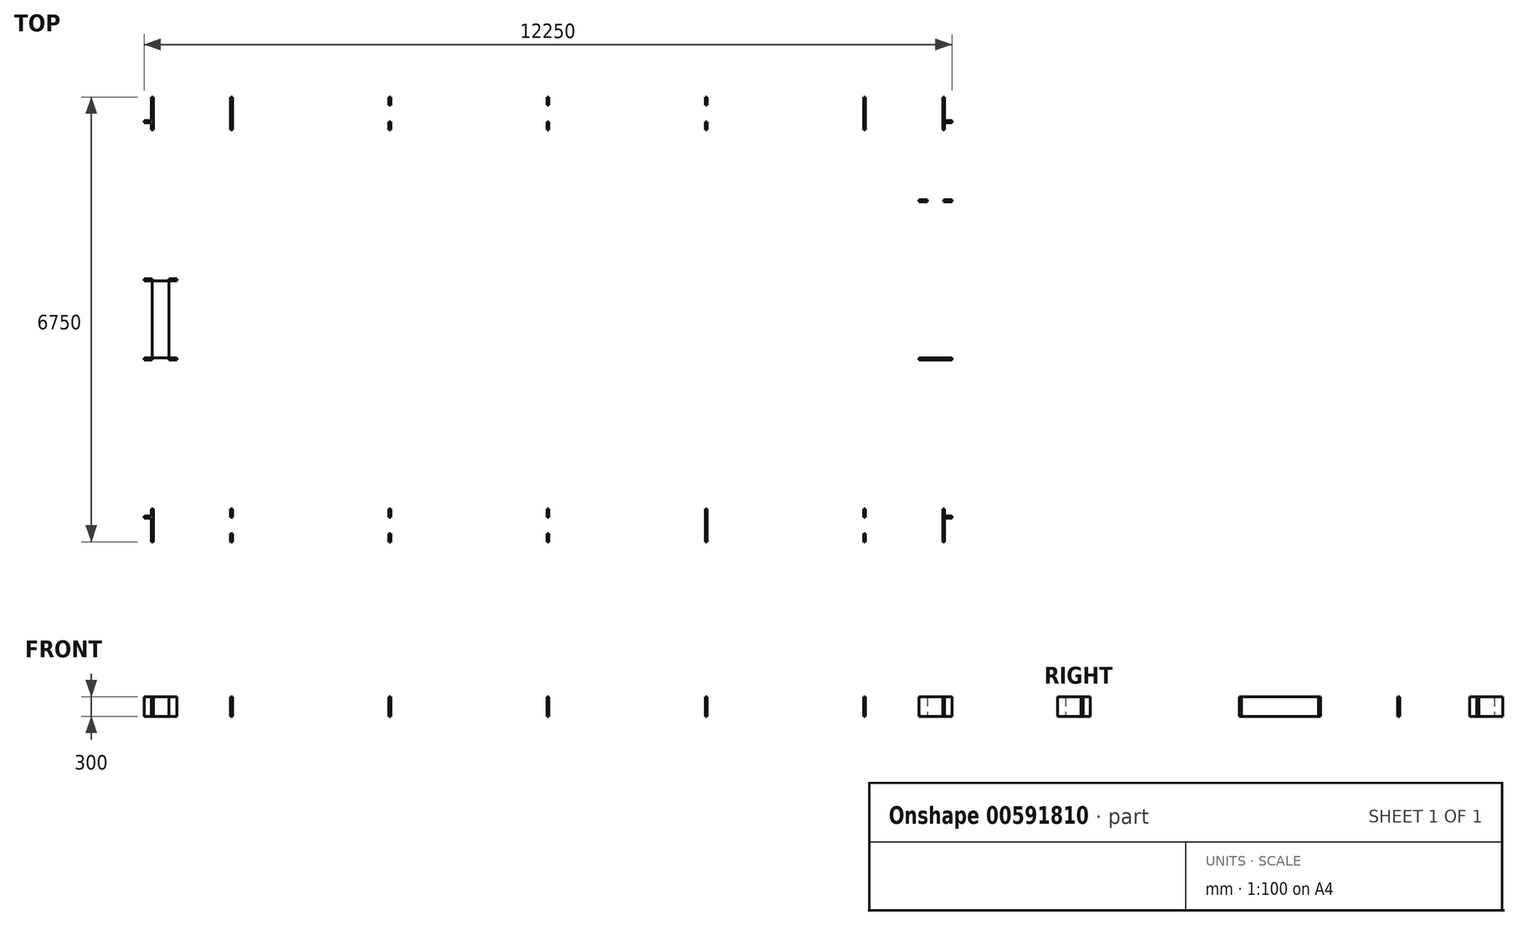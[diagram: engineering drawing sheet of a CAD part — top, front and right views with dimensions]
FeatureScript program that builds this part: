
annotation { "Feature Type Name" : "Feature", "Feature Type Description" : "" }
export const myFeature = defineFeature(function(context is Context, id is Id, definition is map)
    precondition{}
    {
        {
            var Q0;
            Q0=qCreatedBy(makeId("Top.planeOp"),FACE);
            var sketch = newSketch(context, id + "F0", { "sketchPlane" : qUnion([Q0]), "disableImprinting" : false});
            skLineSegment(sketch, "E0.bottom", {"start": v(-5814.67, 3025.3) * mm, "end": v(5685.33, 3025.3) * mm});
            skLineSegment(sketch, "E0.top", {"start": v(-5814.67, -2974.7) * mm, "end": v(5685.33, -2974.7) * mm});
            skLineSegment(sketch, "E0.left", {"start": v(-5814.67, 3025.3) * mm, "end": v(-5814.67, -2974.7) * mm});
            skLineSegment(sketch, "E0.right", {"start": v(5685.33, 3025.3) * mm, "end": v(5685.33, -2974.7) * mm});
            skLineSegment(sketch, "E1.bottom", {"start": v(-5814.67, 3025.3) * mm, "end": v(-6064.67, 3025.3) * mm});
            skLineSegment(sketch, "E1.top", {"start": v(-5814.67, 625.3) * mm, "end": v(-6064.67, 625.3) * mm});
            skLineSegment(sketch, "E1.left", {"start": v(-5814.67, 3025.3) * mm, "end": v(-5814.67, 625.3) * mm});
            skLineSegment(sketch, "E1.right", {"start": v(-6064.67, 3025.3) * mm, "end": v(-6064.67, 625.3) * mm});
            skLineSegment(sketch, "E2.bottom", {"start": v(-6064.67, 625.3) * mm, "end": v(-5814.67, 625.3) * mm});
            skLineSegment(sketch, "E2.top", {"start": v(-6064.67, -574.7) * mm, "end": v(-5814.67, -574.7) * mm});
            skLineSegment(sketch, "E2.left", {"start": v(-6064.67, 625.3) * mm, "end": v(-6064.67, -574.7) * mm});
            skLineSegment(sketch, "E2.right", {"start": v(-5814.67, 625.3) * mm, "end": v(-5814.67, -574.7) * mm});
            skLineSegment(sketch, "E3.bottom", {"start": v(-5814.67, -574.7) * mm, "end": v(-6064.67, -574.7) * mm});
            skLineSegment(sketch, "E3.top", {"start": v(-5814.67, -2974.7) * mm, "end": v(-6064.67, -2974.7) * mm});
            skLineSegment(sketch, "E3.left", {"start": v(-5814.67, -574.7) * mm, "end": v(-5814.67, -2974.7) * mm});
            skLineSegment(sketch, "E3.right", {"start": v(-6064.67, -574.7) * mm, "end": v(-6064.67, -2974.7) * mm});
            skLineSegment(sketch, "E4.bottom", {"start": v(-6064.67, -2974.7) * mm, "end": v(-4864.67, -2974.7) * mm});
            skLineSegment(sketch, "E4.top", {"start": v(-6064.67, -3224.7) * mm, "end": v(-4864.67, -3224.7) * mm});
            skLineSegment(sketch, "E4.left", {"start": v(-6064.67, -2974.7) * mm, "end": v(-6064.67, -3224.7) * mm});
            skLineSegment(sketch, "E4.right", {"start": v(-4864.67, -2974.7) * mm, "end": v(-4864.67, -3224.7) * mm});
            skLineSegment(sketch, "E5.bottom", {"start": v(-4864.67, -2974.7) * mm, "end": v(-2464.67, -2974.7) * mm});
            skLineSegment(sketch, "E5.top", {"start": v(-4864.67, -3224.7) * mm, "end": v(-2464.67, -3224.7) * mm});
            skLineSegment(sketch, "E5.right", {"start": v(-2464.67, -2974.7) * mm, "end": v(-2464.67, -3224.7) * mm});
            skLineSegment(sketch, "E6.bottom", {"start": v(5685.33, -2974.7) * mm, "end": v(5935.33, -2974.7) * mm});
            skLineSegment(sketch, "E6.top", {"start": v(5685.33, -574.7) * mm, "end": v(5935.33, -574.7) * mm});
            skLineSegment(sketch, "E6.left", {"start": v(5685.33, -2974.7) * mm, "end": v(5685.33, -574.7) * mm});
            skLineSegment(sketch, "E6.right", {"start": v(5935.33, -2974.7) * mm, "end": v(5935.33, -574.7) * mm});
            skLineSegment(sketch, "E7.bottom", {"start": v(5935.33, -2974.7) * mm, "end": v(4735.33, -2974.7) * mm});
            skLineSegment(sketch, "E7.top", {"start": v(5935.33, -3224.7) * mm, "end": v(4735.33, -3224.7) * mm});
            skLineSegment(sketch, "E7.left", {"start": v(5935.33, -2974.7) * mm, "end": v(5935.33, -3224.7) * mm});
            skLineSegment(sketch, "E7.right", {"start": v(4735.33, -2974.7) * mm, "end": v(4735.33, -3224.7) * mm});
            skLineSegment(sketch, "E8.bottom", {"start": v(4735.33, -2974.7) * mm, "end": v(2335.33, -2974.7) * mm});
            skLineSegment(sketch, "E8.top", {"start": v(4735.33, -3224.7) * mm, "end": v(2335.33, -3224.7) * mm});
            skLineSegment(sketch, "E8.right", {"start": v(2335.33, -2974.7) * mm, "end": v(2335.33, -3224.7) * mm});
            skLineSegment(sketch, "E9.bottom", {"start": v(2335.33, -2974.7) * mm, "end": v(-64.67, -2974.7) * mm});
            skLineSegment(sketch, "E9.top", {"start": v(2335.33, -3224.7) * mm, "end": v(-64.67, -3224.7) * mm});
            skLineSegment(sketch, "E9.right", {"start": v(-64.67, -2974.7) * mm, "end": v(-64.67, -3224.7) * mm});
            skLineSegment(sketch, "E10.bottom", {"start": v(-2464.67, -2974.7) * mm, "end": v(-64.67, -2974.7) * mm});
            skLineSegment(sketch, "E10.top", {"start": v(-2464.67, -3224.7) * mm, "end": v(-64.67, -3224.7) * mm});
            skLineSegment(sketch, "E11.top", {"start": v(5685.33, 1825.3) * mm, "end": v(5935.33, 1825.3) * mm});
            skLineSegment(sketch, "E11.left", {"start": v(5685.33, -574.7) * mm, "end": v(5685.33, 1825.3) * mm});
            skLineSegment(sketch, "E11.right", {"start": v(5935.33, -574.7) * mm, "end": v(5935.33, 1825.3) * mm});
            skLineSegment(sketch, "E12.top", {"start": v(5685.33, 3025.3) * mm, "end": v(5935.33, 3025.3) * mm});
            skLineSegment(sketch, "E12.left", {"start": v(5685.33, 1825.3) * mm, "end": v(5685.33, 3025.3) * mm});
            skLineSegment(sketch, "E12.right", {"start": v(5935.33, 1825.3) * mm, "end": v(5935.33, 3025.3) * mm});
            skLineSegment(sketch, "E13.bottom", {"start": v(5935.33, 3025.3) * mm, "end": v(4735.33, 3025.3) * mm});
            skLineSegment(sketch, "E13.top", {"start": v(5935.33, 3275.3) * mm, "end": v(4735.33, 3275.3) * mm});
            skLineSegment(sketch, "E13.left", {"start": v(5935.33, 3025.3) * mm, "end": v(5935.33, 3275.3) * mm});
            skLineSegment(sketch, "E13.right", {"start": v(4735.33, 3025.3) * mm, "end": v(4735.33, 3275.3) * mm});
            skLineSegment(sketch, "E14.bottom", {"start": v(-6064.67, 3025.3) * mm, "end": v(-4864.67, 3025.3) * mm});
            skLineSegment(sketch, "E14.top", {"start": v(-6064.67, 3275.3) * mm, "end": v(-4864.67, 3275.3) * mm});
            skLineSegment(sketch, "E14.left", {"start": v(-6064.67, 3025.3) * mm, "end": v(-6064.67, 3275.3) * mm});
            skLineSegment(sketch, "E14.right", {"start": v(-4864.67, 3025.3) * mm, "end": v(-4864.67, 3275.3) * mm});
            skLineSegment(sketch, "E15.bottom", {"start": v(-4864.67, 3025.3) * mm, "end": v(-2464.67, 3025.3) * mm});
            skLineSegment(sketch, "E15.top", {"start": v(-4864.67, 3275.3) * mm, "end": v(-2464.67, 3275.3) * mm});
            skLineSegment(sketch, "E15.right", {"start": v(-2464.67, 3025.3) * mm, "end": v(-2464.67, 3275.3) * mm});
            skLineSegment(sketch, "E16.bottom", {"start": v(4735.33, 3025.3) * mm, "end": v(2335.33, 3025.3) * mm});
            skLineSegment(sketch, "E16.top", {"start": v(4735.33, 3275.3) * mm, "end": v(2335.33, 3275.3) * mm});
            skLineSegment(sketch, "E16.right", {"start": v(2335.33, 3025.3) * mm, "end": v(2335.33, 3275.3) * mm});
            skLineSegment(sketch, "E17.bottom", {"start": v(-2464.67, 3025.3) * mm, "end": v(-64.67, 3025.3) * mm});
            skLineSegment(sketch, "E17.top", {"start": v(-2464.67, 3275.3) * mm, "end": v(-64.67, 3275.3) * mm});
            skLineSegment(sketch, "E17.right", {"start": v(-64.67, 3025.3) * mm, "end": v(-64.67, 3275.3) * mm});
            skLineSegment(sketch, "E18.bottom", {"start": v(2335.33, 3025.3) * mm, "end": v(-64.67, 3025.3) * mm});
            skLineSegment(sketch, "E18.top", {"start": v(2335.33, 3275.3) * mm, "end": v(-64.67, 3275.3) * mm});
            skLineSegment(sketch, "E19.bottom", {"start": v(-4849.67, 2900.3) * mm, "end": v(-4879.67, 2900.3) * mm});
            skLineSegment(sketch, "E19.top", {"start": v(-4849.67, 3400.3) * mm, "end": v(-4879.67, 3400.3) * mm});
            skLineSegment(sketch, "E19.left", {"start": v(-4849.67, 2900.3) * mm, "end": v(-4849.67, 3400.3) * mm});
            skLineSegment(sketch, "E19.right", {"start": v(-4879.67, 2900.3) * mm, "end": v(-4879.67, 3400.3) * mm});
            skPoint(sketch, "E19.middle", {"position": v(-4864.67, 3150.3) * mm});
            skLineSegment(sketch, "E20.bottom", {"start": v(-6079.67, 2900.3) * mm, "end": v(-6049.67, 2900.3) * mm});
            skLineSegment(sketch, "E20.top", {"start": v(-6079.67, 3400.3) * mm, "end": v(-6049.67, 3400.3) * mm});
            skLineSegment(sketch, "E20.left", {"start": v(-6079.67, 2900.3) * mm, "end": v(-6079.67, 3400.3) * mm});
            skLineSegment(sketch, "E20.right", {"start": v(-6049.67, 2900.3) * mm, "end": v(-6049.67, 3400.3) * mm});
            skPoint(sketch, "E20.middle", {"position": v(-6064.67, 3150.3) * mm});
            skLineSegment(sketch, "E21.bottom", {"start": v(-5689.67, 610.3) * mm, "end": v(-6189.67, 610.3) * mm});
            skLineSegment(sketch, "E21.top", {"start": v(-5689.67, 640.3) * mm, "end": v(-6189.67, 640.3) * mm});
            skLineSegment(sketch, "E21.left", {"start": v(-5689.67, 610.3) * mm, "end": v(-5689.67, 640.3) * mm});
            skLineSegment(sketch, "E21.right", {"start": v(-6189.67, 610.3) * mm, "end": v(-6189.67, 640.3) * mm});
            skPoint(sketch, "E21.middle", {"position": v(-5939.67, 625.3) * mm});
            skLineSegment(sketch, "E22.bottom", {"start": v(-5689.67, -559.7) * mm, "end": v(-6189.67, -559.7) * mm});
            skLineSegment(sketch, "E22.top", {"start": v(-5689.67, -589.7) * mm, "end": v(-6189.67, -589.7) * mm});
            skLineSegment(sketch, "E22.left", {"start": v(-5689.67, -559.7) * mm, "end": v(-5689.67, -589.7) * mm});
            skLineSegment(sketch, "E22.right", {"start": v(-6189.67, -559.7) * mm, "end": v(-6189.67, -589.7) * mm});
            skPoint(sketch, "E22.middle", {"position": v(-5939.67, -574.7) * mm});
            skLineSegment(sketch, "E23.bottom", {"start": v(-6189.67, -2959.7) * mm, "end": v(-5689.67, -2959.7) * mm});
            skLineSegment(sketch, "E23.top", {"start": v(-6189.67, -2989.7) * mm, "end": v(-5689.67, -2989.7) * mm});
            skLineSegment(sketch, "E23.left", {"start": v(-6189.67, -2959.7) * mm, "end": v(-6189.67, -2989.7) * mm});
            skLineSegment(sketch, "E23.right", {"start": v(-5689.67, -2959.7) * mm, "end": v(-5689.67, -2989.7) * mm});
            skPoint(sketch, "E23.middle", {"position": v(-5939.67, -2974.7) * mm});
            skLineSegment(sketch, "E24.bottom", {"start": v(-4849.67, -2849.7) * mm, "end": v(-4879.67, -2849.7) * mm});
            skLineSegment(sketch, "E24.top", {"start": v(-4849.67, -3349.7) * mm, "end": v(-4879.67, -3349.7) * mm});
            skLineSegment(sketch, "E24.left", {"start": v(-4849.67, -2849.7) * mm, "end": v(-4849.67, -3349.7) * mm});
            skLineSegment(sketch, "E24.right", {"start": v(-4879.67, -2849.7) * mm, "end": v(-4879.67, -3349.7) * mm});
            skPoint(sketch, "E24.middle", {"position": v(-4864.67, -3099.7) * mm});
            skLineSegment(sketch, "E25.bottom", {"start": v(-2479.67, -2849.7) * mm, "end": v(-2449.67, -2849.7) * mm});
            skLineSegment(sketch, "E25.top", {"start": v(-2479.67, -3349.7) * mm, "end": v(-2449.67, -3349.7) * mm});
            skLineSegment(sketch, "E25.left", {"start": v(-2479.67, -2849.7) * mm, "end": v(-2479.67, -3349.7) * mm});
            skLineSegment(sketch, "E25.right", {"start": v(-2449.67, -2849.7) * mm, "end": v(-2449.67, -3349.7) * mm});
            skPoint(sketch, "E25.middle", {"position": v(-2464.67, -3099.7) * mm});
            skLineSegment(sketch, "E26.bottom", {"start": v(-79.67, -2849.7) * mm, "end": v(-49.67, -2849.7) * mm});
            skLineSegment(sketch, "E26.top", {"start": v(-79.67, -3349.7) * mm, "end": v(-49.67, -3349.7) * mm});
            skLineSegment(sketch, "E26.left", {"start": v(-79.67, -2849.7) * mm, "end": v(-79.67, -3349.7) * mm});
            skLineSegment(sketch, "E26.right", {"start": v(-49.67, -2849.7) * mm, "end": v(-49.67, -3349.7) * mm});
            skPoint(sketch, "E26.middle", {"position": v(-64.67, -3099.7) * mm});
            skLineSegment(sketch, "E27.bottom", {"start": v(2320.33, -2849.7) * mm, "end": v(2350.33, -2849.7) * mm});
            skLineSegment(sketch, "E27.top", {"start": v(2320.33, -3349.7) * mm, "end": v(2350.33, -3349.7) * mm});
            skLineSegment(sketch, "E27.left", {"start": v(2320.33, -2849.7) * mm, "end": v(2320.33, -3349.7) * mm});
            skLineSegment(sketch, "E27.right", {"start": v(2350.33, -2849.7) * mm, "end": v(2350.33, -3349.7) * mm});
            skPoint(sketch, "E27.middle", {"position": v(2335.33, -3099.7) * mm});
            skLineSegment(sketch, "E28.bottom", {"start": v(4720.33, -2849.7) * mm, "end": v(4750.33, -2849.7) * mm});
            skLineSegment(sketch, "E28.top", {"start": v(4720.33, -3349.7) * mm, "end": v(4750.33, -3349.7) * mm});
            skLineSegment(sketch, "E28.left", {"start": v(4720.33, -2849.7) * mm, "end": v(4720.33, -3349.7) * mm});
            skLineSegment(sketch, "E28.right", {"start": v(4750.33, -2849.7) * mm, "end": v(4750.33, -3349.7) * mm});
            skPoint(sketch, "E28.middle", {"position": v(4735.33, -3099.7) * mm});
            skLineSegment(sketch, "E29.bottom", {"start": v(5950.33, -3349.7) * mm, "end": v(5920.33, -3349.7) * mm});
            skLineSegment(sketch, "E29.top", {"start": v(5950.33, -2849.7) * mm, "end": v(5920.33, -2849.7) * mm});
            skLineSegment(sketch, "E29.left", {"start": v(5950.33, -3349.7) * mm, "end": v(5950.33, -2849.7) * mm});
            skLineSegment(sketch, "E29.right", {"start": v(5920.33, -3349.7) * mm, "end": v(5920.33, -2849.7) * mm});
            skPoint(sketch, "E29.middle", {"position": v(5935.33, -3099.7) * mm});
            skLineSegment(sketch, "E30.bottom", {"start": v(6060.33, -2959.7) * mm, "end": v(5560.33, -2959.7) * mm});
            skLineSegment(sketch, "E30.top", {"start": v(6060.33, -2989.7) * mm, "end": v(5560.33, -2989.7) * mm});
            skLineSegment(sketch, "E30.left", {"start": v(6060.33, -2959.7) * mm, "end": v(6060.33, -2989.7) * mm});
            skLineSegment(sketch, "E30.right", {"start": v(5560.33, -2959.7) * mm, "end": v(5560.33, -2989.7) * mm});
            skPoint(sketch, "E30.middle", {"position": v(5810.33, -2974.7) * mm});
            skLineSegment(sketch, "E31.bottom", {"start": v(6060.33, -589.7) * mm, "end": v(5560.33, -589.7) * mm});
            skLineSegment(sketch, "E31.top", {"start": v(6060.33, -559.7) * mm, "end": v(5560.33, -559.7) * mm});
            skLineSegment(sketch, "E31.left", {"start": v(6060.33, -589.7) * mm, "end": v(6060.33, -559.7) * mm});
            skLineSegment(sketch, "E31.right", {"start": v(5560.33, -589.7) * mm, "end": v(5560.33, -559.7) * mm});
            skPoint(sketch, "E31.middle", {"position": v(5810.33, -574.7) * mm});
            skLineSegment(sketch, "E32.bottom", {"start": v(6060.33, 1840.3) * mm, "end": v(5560.33, 1840.3) * mm});
            skLineSegment(sketch, "E32.top", {"start": v(6060.33, 1810.3) * mm, "end": v(5560.33, 1810.3) * mm});
            skLineSegment(sketch, "E32.left", {"start": v(6060.33, 1840.3) * mm, "end": v(6060.33, 1810.3) * mm});
            skLineSegment(sketch, "E32.right", {"start": v(5560.33, 1840.3) * mm, "end": v(5560.33, 1810.3) * mm});
            skPoint(sketch, "E32.middle", {"position": v(5810.33, 1825.3) * mm});
            skLineSegment(sketch, "E33.bottom", {"start": v(6060.33, 3040.3) * mm, "end": v(5560.33, 3040.3) * mm});
            skLineSegment(sketch, "E33.top", {"start": v(6060.33, 3010.3) * mm, "end": v(5560.33, 3010.3) * mm});
            skLineSegment(sketch, "E33.left", {"start": v(6060.33, 3040.3) * mm, "end": v(6060.33, 3010.3) * mm});
            skLineSegment(sketch, "E33.right", {"start": v(5560.33, 3040.3) * mm, "end": v(5560.33, 3010.3) * mm});
            skPoint(sketch, "E33.middle", {"position": v(5810.33, 3025.3) * mm});
            skLineSegment(sketch, "E34.bottom", {"start": v(4750.33, 2900.3) * mm, "end": v(4720.33, 2900.3) * mm});
            skLineSegment(sketch, "E34.top", {"start": v(4750.33, 3400.3) * mm, "end": v(4720.33, 3400.3) * mm});
            skLineSegment(sketch, "E34.left", {"start": v(4750.33, 2900.3) * mm, "end": v(4750.33, 3400.3) * mm});
            skLineSegment(sketch, "E34.right", {"start": v(4720.33, 2900.3) * mm, "end": v(4720.33, 3400.3) * mm});
            skPoint(sketch, "E34.middle", {"position": v(4735.33, 3150.3) * mm});
            skLineSegment(sketch, "E35.bottom", {"start": v(2320.33, 3400.3) * mm, "end": v(2350.33, 3400.3) * mm});
            skLineSegment(sketch, "E35.top", {"start": v(2320.33, 2900.3) * mm, "end": v(2350.33, 2900.3) * mm});
            skLineSegment(sketch, "E35.left", {"start": v(2320.33, 3400.3) * mm, "end": v(2320.33, 2900.3) * mm});
            skLineSegment(sketch, "E35.right", {"start": v(2350.33, 3400.3) * mm, "end": v(2350.33, 2900.3) * mm});
            skPoint(sketch, "E35.middle", {"position": v(2335.33, 3150.3) * mm});
            skLineSegment(sketch, "E36.bottom", {"start": v(-49.67, 3400.3) * mm, "end": v(-79.67, 3400.3) * mm});
            skLineSegment(sketch, "E36.top", {"start": v(-49.67, 2900.3) * mm, "end": v(-79.67, 2900.3) * mm});
            skLineSegment(sketch, "E36.left", {"start": v(-49.67, 3400.3) * mm, "end": v(-49.67, 2900.3) * mm});
            skLineSegment(sketch, "E36.right", {"start": v(-79.67, 3400.3) * mm, "end": v(-79.67, 2900.3) * mm});
            skPoint(sketch, "E36.middle", {"position": v(-64.67, 3150.3) * mm});
            skLineSegment(sketch, "E37.bottom", {"start": v(-2479.67, 3400.3) * mm, "end": v(-2449.67, 3400.3) * mm});
            skLineSegment(sketch, "E37.top", {"start": v(-2479.67, 2900.3) * mm, "end": v(-2449.67, 2900.3) * mm});
            skLineSegment(sketch, "E37.left", {"start": v(-2479.67, 3400.3) * mm, "end": v(-2479.67, 2900.3) * mm});
            skLineSegment(sketch, "E37.right", {"start": v(-2449.67, 3400.3) * mm, "end": v(-2449.67, 2900.3) * mm});
            skPoint(sketch, "E37.middle", {"position": v(-2464.67, 3150.3) * mm});
            skLineSegment(sketch, "E38.bottom", {"start": v(-5689.67, 3010.3) * mm, "end": v(-6189.67, 3010.3) * mm});
            skLineSegment(sketch, "E38.top", {"start": v(-5689.67, 3040.3) * mm, "end": v(-6189.67, 3040.3) * mm});
            skLineSegment(sketch, "E38.left", {"start": v(-5689.67, 3010.3) * mm, "end": v(-5689.67, 3040.3) * mm});
            skLineSegment(sketch, "E38.right", {"start": v(-6189.67, 3010.3) * mm, "end": v(-6189.67, 3040.3) * mm});
            skPoint(sketch, "E38.middle", {"position": v(-5939.67, 3025.3) * mm});
            skLineSegment(sketch, "E39.bottom", {"start": v(-6079.67, -2849.7) * mm, "end": v(-6049.67, -2849.7) * mm});
            skLineSegment(sketch, "E39.top", {"start": v(-6079.67, -3349.7) * mm, "end": v(-6049.67, -3349.7) * mm});
            skLineSegment(sketch, "E39.left", {"start": v(-6079.67, -2849.7) * mm, "end": v(-6079.67, -3349.7) * mm});
            skLineSegment(sketch, "E39.right", {"start": v(-6049.67, -2849.7) * mm, "end": v(-6049.67, -3349.7) * mm});
            skPoint(sketch, "E39.middle", {"position": v(-6064.67, -3099.7) * mm});
            skLineSegment(sketch, "E40.bottom", {"start": v(5950.33, 3400.3) * mm, "end": v(5920.33, 3400.3) * mm});
            skLineSegment(sketch, "E40.top", {"start": v(5950.33, 2900.3) * mm, "end": v(5920.33, 2900.3) * mm});
            skLineSegment(sketch, "E40.left", {"start": v(5950.33, 3400.3) * mm, "end": v(5950.33, 2900.3) * mm});
            skLineSegment(sketch, "E40.right", {"start": v(5920.33, 3400.3) * mm, "end": v(5920.33, 2900.3) * mm});
            skPoint(sketch, "E40.middle", {"position": v(5935.33, 3150.3) * mm});
            skSolve(sketch);
        }
        {
            var Q0;
            {var subQ0=sQuery(id+"F0.wireOp",EDGE,"E25.right");var subQ1=sQuery(id+"F0.wireOp",EDGE,"E10.bottom");var subQ2=makeQuery(id+"F0.imprint","INTERSECT",VERTEX,{"derivedFrom":[subQ1,subQ0]});Q0=makeQuery(id+"F0.imprint","IMPRINT",FACE,{"disambiguationData":[TD([[makeQuery(id+"F0.imprint","IMPRINT",EDGE,{"disambiguationData":[TD([[subQ2,-1.0]])],"derivedFrom":subQ1}),-1.0]])]});}
            var Q1;
            {var subQ0=sQuery(id+"F0.wireOp",EDGE,"E37.right");var subQ1=sQuery(id+"F0.wireOp",EDGE,"E17.bottom");var subQ2=makeQuery(id+"F0.imprint","INTERSECT",VERTEX,{"derivedFrom":[subQ1,subQ0]});Q1=makeQuery(id+"F0.imprint","IMPRINT",FACE,{"disambiguationData":[TD([[makeQuery(id+"F0.imprint","IMPRINT",EDGE,{"disambiguationData":[TD([[subQ2,-1.0]])],"derivedFrom":subQ1}),1.0]])]});}
            var Q2;
            {var subQ0=sQuery(id+"F0.wireOp",EDGE,"E33.right");var subQ3=sQuery(id+"F0.wireOp",EDGE,"E13.bottom");var subQ4=makeQuery(id+"F0.imprint","INTERSECT",VERTEX,{"derivedFrom":[subQ3,subQ0]});Q2=makeQuery(id+"F0.imprint","IMPRINT",FACE,{"disambiguationData":[TD([[makeQuery(id+"F0.imprint","IMPRINT",EDGE,{"disambiguationData":[TD([[subQ4,-1.0]])],"derivedFrom":subQ3}),-1.0]])]});}
            var Q3;
            {var subQ3=sQuery(id+"F0.wireOp",EDGE,"E14.bottom");var subQ9=sQuery(id+"F0.wireOp",EDGE,"E38.left");var subQ10=makeQuery(id+"F0.imprint","INTERSECT",VERTEX,{"derivedFrom":[subQ3,subQ9]});Q3=makeQuery(id+"F0.imprint","IMPRINT",FACE,{"disambiguationData":[TD([[makeQuery(id+"F0.imprint","IMPRINT",EDGE,{"disambiguationData":[TD([[subQ10,-1.0]])],"derivedFrom":subQ3}),1.0]])]});}
            var Q4;
            {var subQ5=sQuery(id+"F0.wireOp",EDGE,"E30.right");var subQ6=sQuery(id+"F0.wireOp",EDGE,"E7.bottom");var subQ7=makeQuery(id+"F0.imprint","INTERSECT",VERTEX,{"derivedFrom":[subQ6,subQ5]});Q4=makeQuery(id+"F0.imprint","IMPRINT",FACE,{"disambiguationData":[TD([[makeQuery(id+"F0.imprint","IMPRINT",EDGE,{"disambiguationData":[TD([[subQ7,-1.0]])],"derivedFrom":subQ6}),1.0]])]});}
            var Q5;
            {var subQ0=sQuery(id+"F0.wireOp",EDGE,"E27.left");var subQ1=sQuery(id+"F0.wireOp",EDGE,"E9.bottom");var subQ2=makeQuery(id+"F0.imprint","INTERSECT",VERTEX,{"derivedFrom":[subQ1,subQ0]});Q5=makeQuery(id+"F0.imprint","IMPRINT",FACE,{"disambiguationData":[TD([[makeQuery(id+"F0.imprint","IMPRINT",EDGE,{"disambiguationData":[TD([[subQ2,-1.0]])],"derivedFrom":subQ1}),1.0]])]});}
            var Q6;
            {var subQ0=sQuery(id+"F0.wireOp",EDGE,"E24.left");var subQ1=sQuery(id+"F0.wireOp",EDGE,"E5.bottom");var subQ2=makeQuery(id+"F0.imprint","INTERSECT",VERTEX,{"derivedFrom":[subQ1,subQ0]});Q6=makeQuery(id+"F0.imprint","IMPRINT",FACE,{"disambiguationData":[TD([[makeQuery(id+"F0.imprint","IMPRINT",EDGE,{"disambiguationData":[TD([[subQ2,-1.0]])],"derivedFrom":subQ1}),-1.0]])]});}
            var Q7;
            {var subQ0=sQuery(id+"F0.wireOp",EDGE,"E19.left");var subQ1=sQuery(id+"F0.wireOp",EDGE,"E15.bottom");var subQ2=makeQuery(id+"F0.imprint","INTERSECT",VERTEX,{"derivedFrom":[subQ1,subQ0]});Q7=makeQuery(id+"F0.imprint","IMPRINT",FACE,{"disambiguationData":[TD([[makeQuery(id+"F0.imprint","IMPRINT",EDGE,{"disambiguationData":[TD([[subQ2,-1.0]])],"derivedFrom":subQ1}),1.0]])]});}
            var Q8;
            {var subQ1=sQuery(id+"F0.wireOp",EDGE,"E3.left");var subQ5=sQuery(id+"F0.wireOp",EDGE,"E22.top");var subQ8=makeQuery(id+"F0.imprint","INTERSECT",VERTEX,{"derivedFrom":[subQ1,subQ5]});Q8=makeQuery(id+"F0.imprint","IMPRINT",FACE,{"disambiguationData":[TD([[makeQuery(id+"F0.imprint","IMPRINT",EDGE,{"disambiguationData":[TD([[subQ8,-1.0]])],"derivedFrom":subQ1}),-1.0]])]});}
            var Q9;
            {var subQ0=sQuery(id+"F0.wireOp",EDGE,"E21.bottom");var subQ1=sQuery(id+"F0.wireOp",EDGE,"E2.left");var subQ2=makeQuery(id+"F0.imprint","INTERSECT",VERTEX,{"derivedFrom":[subQ1,subQ0]});Q9=makeQuery(id+"F0.imprint","IMPRINT",FACE,{"disambiguationData":[TD([[makeQuery(id+"F0.imprint","IMPRINT",EDGE,{"disambiguationData":[TD([[subQ2,-1.0]])],"derivedFrom":subQ1}),1.0]])]});}
            var Q10;
            {var subQ0=sQuery(id+"F0.wireOp",EDGE,"E34.right");var subQ1=sQuery(id+"F0.wireOp",EDGE,"E16.bottom");var subQ2=makeQuery(id+"F0.imprint","INTERSECT",VERTEX,{"derivedFrom":[subQ1,subQ0]});Q10=makeQuery(id+"F0.imprint","IMPRINT",FACE,{"disambiguationData":[TD([[makeQuery(id+"F0.imprint","IMPRINT",EDGE,{"disambiguationData":[TD([[subQ2,-1.0]])],"derivedFrom":subQ1}),-1.0]])]});}
            var Q11;
            {var subQ0=sQuery(id+"F0.wireOp",EDGE,"E31.top");var subQ1=sQuery(id+"F0.wireOp",EDGE,"E11.left");var subQ2=makeQuery(id+"F0.imprint","INTERSECT",VERTEX,{"derivedFrom":[subQ1,subQ0]});Q11=makeQuery(id+"F0.imprint","IMPRINT",FACE,{"disambiguationData":[TD([[makeQuery(id+"F0.imprint","IMPRINT",EDGE,{"disambiguationData":[TD([[subQ2,-1.0]])],"derivedFrom":subQ1}),-1.0]])]});}
            var Q12;
            {var subQ7=sQuery(id+"F0.wireOp",EDGE,"E6.left");var subQ9=sQuery(id+"F0.wireOp",EDGE,"E30.bottom");var subQ11=makeQuery(id+"F0.imprint","INTERSECT",VERTEX,{"derivedFrom":[subQ7,subQ9]});Q12=makeQuery(id+"F0.imprint","IMPRINT",FACE,{"disambiguationData":[TD([[makeQuery(id+"F0.imprint","IMPRINT",EDGE,{"disambiguationData":[TD([[subQ11,-1.0]])],"derivedFrom":subQ7}),-1.0]])]});}
            var Q13;
            {var subQ5=sQuery(id+"F0.wireOp",EDGE,"E38.bottom");var subQ6=sQuery(id+"F0.wireOp",EDGE,"E1.left");var subQ7=makeQuery(id+"F0.imprint","INTERSECT",VERTEX,{"derivedFrom":[subQ6,subQ5]});Q13=makeQuery(id+"F0.imprint","IMPRINT",FACE,{"disambiguationData":[TD([[makeQuery(id+"F0.imprint","IMPRINT",EDGE,{"disambiguationData":[TD([[subQ7,-1.0]])],"derivedFrom":subQ6}),-1.0]])]});}
            var Q14;
            {var subQ0=sQuery(id+"F0.wireOp",EDGE,"E35.left");var subQ1=sQuery(id+"F0.wireOp",EDGE,"E18.bottom");var subQ2=makeQuery(id+"F0.imprint","INTERSECT",VERTEX,{"derivedFrom":[subQ1,subQ0]});Q14=makeQuery(id+"F0.imprint","IMPRINT",FACE,{"disambiguationData":[TD([[makeQuery(id+"F0.imprint","IMPRINT",EDGE,{"disambiguationData":[TD([[subQ2,-1.0]])],"derivedFrom":subQ1}),-1.0]])]});}
            var Q15;
            {var subQ0=sQuery(id+"F0.wireOp",EDGE,"E23.right");var subQ3=sQuery(id+"F0.wireOp",EDGE,"E4.bottom");var subQ4=makeQuery(id+"F0.imprint","INTERSECT",VERTEX,{"derivedFrom":[subQ3,subQ0]});Q15=makeQuery(id+"F0.imprint","IMPRINT",FACE,{"disambiguationData":[TD([[makeQuery(id+"F0.imprint","IMPRINT",EDGE,{"disambiguationData":[TD([[subQ4,-1.0]])],"derivedFrom":subQ3}),-1.0]])]});}
            var Q16;
            {var subQ0=sQuery(id+"F0.wireOp",EDGE,"E28.left");var subQ1=sQuery(id+"F0.wireOp",EDGE,"E8.bottom");var subQ2=makeQuery(id+"F0.imprint","INTERSECT",VERTEX,{"derivedFrom":[subQ1,subQ0]});Q16=makeQuery(id+"F0.imprint","IMPRINT",FACE,{"disambiguationData":[TD([[makeQuery(id+"F0.imprint","IMPRINT",EDGE,{"disambiguationData":[TD([[subQ2,-1.0]])],"derivedFrom":subQ1}),1.0]])]});}
            var Q17;
            {var subQ0=sQuery(id+"F0.wireOp",EDGE,"E32.bottom");var subQ3=sQuery(id+"F0.wireOp",EDGE,"E12.left");var subQ4=makeQuery(id+"F0.imprint","INTERSECT",VERTEX,{"derivedFrom":[subQ3,subQ0]});Q17=makeQuery(id+"F0.imprint","IMPRINT",FACE,{"disambiguationData":[TD([[makeQuery(id+"F0.imprint","IMPRINT",EDGE,{"disambiguationData":[TD([[subQ4,-1.0]])],"derivedFrom":subQ3}),-1.0]])]});}
            var Q18;
            {var subQ1=sQuery(id+"F0.wireOp",EDGE,"E29.bottom");Q18=makeQuery(id+"F0.imprint","IMPRINT",FACE,{"disambiguationData":[TD([[makeQuery(id+"F0.imprint","IMPRINT",EDGE,{"derivedFrom":subQ1}),-1.0]])]});}
            var Q19;
            {var subQ0=sQuery(id+"F0.wireOp",EDGE,"E15.right");Q19=makeQuery(id+"F0.imprint","IMPRINT",FACE,{"disambiguationData":[TD([[makeQuery(id+"F0.imprint","IMPRINT",EDGE,{"derivedFrom":subQ0}),-1.0]])]});}
            var Q20;
            {var subQ0=sQuery(id+"F0.wireOp",EDGE,"E40.bottom");Q20=makeQuery(id+"F0.imprint","IMPRINT",FACE,{"disambiguationData":[TD([[makeQuery(id+"F0.imprint","IMPRINT",EDGE,{"derivedFrom":subQ0}),1.0]])]});}
            var Q21;
            {var subQ0=sQuery(id+"F0.wireOp",EDGE,"E4.right");Q21=makeQuery(id+"F0.imprint","IMPRINT",FACE,{"disambiguationData":[TD([[makeQuery(id+"F0.imprint","IMPRINT",EDGE,{"derivedFrom":subQ0}),-1.0]])]});}
            var Q22;
            {var subQ1=sQuery(id+"F0.wireOp",EDGE,"E27.bottom");Q22=makeQuery(id+"F0.imprint","IMPRINT",FACE,{"disambiguationData":[TD([[makeQuery(id+"F0.imprint","IMPRINT",EDGE,{"derivedFrom":subQ1}),-1.0]])]});}
            var Q23;
            {var subQ0=sQuery(id+"F0.wireOp",EDGE,"E8.right");Q23=makeQuery(id+"F0.imprint","IMPRINT",FACE,{"disambiguationData":[TD([[makeQuery(id+"F0.imprint","IMPRINT",EDGE,{"derivedFrom":subQ0}),1.0]])]});}
            var Q24;
            {var subQ1=sQuery(id+"F0.wireOp",EDGE,"E27.top");Q24=makeQuery(id+"F0.imprint","IMPRINT",FACE,{"disambiguationData":[TD([[makeQuery(id+"F0.imprint","IMPRINT",EDGE,{"derivedFrom":subQ1}),1.0]])]});}
            var Q25;
            {var subQ0=sQuery(id+"F0.wireOp",EDGE,"E29.top");var subQ1=sQuery(id+"F0.wireOp",EDGE,"E6.right");var subQ2=makeQuery(id+"F0.imprint","INTERSECT",VERTEX,{"derivedFrom":[subQ1,subQ0]});Q25=makeQuery(id+"F0.imprint","IMPRINT",FACE,{"disambiguationData":[TD([[makeQuery(id+"F0.imprint","IMPRINT",EDGE,{"disambiguationData":[TD([[subQ2,1.0]])],"derivedFrom":subQ1}),-1.0]])]});}
            var Q26;
            {var subQ1=sQuery(id+"F0.wireOp",EDGE,"E24.top");Q26=makeQuery(id+"F0.imprint","IMPRINT",FACE,{"disambiguationData":[TD([[makeQuery(id+"F0.imprint","IMPRINT",EDGE,{"derivedFrom":subQ1}),-1.0]])]});}
            var Q27;
            {var subQ1=sQuery(id+"F0.wireOp",EDGE,"E25.top");Q27=makeQuery(id+"F0.imprint","IMPRINT",FACE,{"disambiguationData":[TD([[makeQuery(id+"F0.imprint","IMPRINT",EDGE,{"derivedFrom":subQ1}),1.0]])]});}
            var Q28;
            {var subQ0=sQuery(id+"F0.wireOp",EDGE,"E24.bottom");Q28=makeQuery(id+"F0.imprint","IMPRINT",FACE,{"disambiguationData":[TD([[makeQuery(id+"F0.imprint","IMPRINT",EDGE,{"derivedFrom":subQ0}),1.0]])]});}
            var Q29;
            {var subQ0=sQuery(id+"F0.wireOp",EDGE,"E5.right");Q29=makeQuery(id+"F0.imprint","IMPRINT",FACE,{"disambiguationData":[TD([[makeQuery(id+"F0.imprint","IMPRINT",EDGE,{"derivedFrom":subQ0}),1.0]])]});}
            var Q30;
            {var subQ0=sQuery(id+"F0.wireOp",EDGE,"E7.left");var subQ1=sQuery(id+"F0.wireOp",EDGE,"E7.top");var subQ2=makeQuery(id+"F0.imprint","INTERSECT",VERTEX,{"derivedFrom":[subQ1,subQ0]});Q30=makeQuery(id+"F0.imprint","IMPRINT",FACE,{"disambiguationData":[TD([[makeQuery(id+"F0.imprint","IMPRINT",EDGE,{"disambiguationData":[TD([[subQ2,-1.0]])],"derivedFrom":subQ1}),-1.0]])]});}
            var Q31;
            {var subQ0=sQuery(id+"F0.wireOp",EDGE,"E7.bottom");var subQ1=sQuery(id+"F0.wireOp",EDGE,"E6.left");var subQ2=makeQuery(id+"F0.imprint","INTERSECT",VERTEX,{"derivedFrom":[subQ1,subQ0]});Q31=makeQuery(id+"F0.imprint","IMPRINT",FACE,{"disambiguationData":[TD([[makeQuery(id+"F0.imprint","IMPRINT",EDGE,{"disambiguationData":[TD([[subQ2,-1.0]])],"derivedFrom":subQ1}),-1.0]])]});}
            var Q32;
            {var subQ0=sQuery(id+"F0.wireOp",EDGE,"E13.right");Q32=makeQuery(id+"F0.imprint","IMPRINT",FACE,{"disambiguationData":[TD([[makeQuery(id+"F0.imprint","IMPRINT",EDGE,{"derivedFrom":subQ0}),1.0]])]});}
            var Q33;
            {var subQ5=sQuery(id+"F0.wireOp",EDGE,"E7.bottom");var subQ7=makeQuery(id+"F0.imprint","INTERSECT",VERTEX,{"derivedFrom":[sQuery(id+"F0.wireOp",EDGE,"E6.left"),subQ5]});Q33=makeQuery(id+"F0.imprint","IMPRINT",FACE,{"disambiguationData":[TD([[makeQuery(id+"F0.imprint","IMPRINT",EDGE,{"disambiguationData":[TD([[subQ7,1.0]])],"derivedFrom":subQ5}),1.0]])]});}
            var Q34;
            {var subQ1=sQuery(id+"F0.wireOp",EDGE,"E28.bottom");Q34=makeQuery(id+"F0.imprint","IMPRINT",FACE,{"disambiguationData":[TD([[makeQuery(id+"F0.imprint","IMPRINT",EDGE,{"derivedFrom":subQ1}),-1.0]])]});}
            var Q35;
            {var subQ1=sQuery(id+"F0.wireOp",EDGE,"E37.top");Q35=makeQuery(id+"F0.imprint","IMPRINT",FACE,{"disambiguationData":[TD([[makeQuery(id+"F0.imprint","IMPRINT",EDGE,{"derivedFrom":subQ1}),1.0]])]});}
            var Q36;
            {var subQ0=sQuery(id+"F0.wireOp",EDGE,"E9.right");Q36=makeQuery(id+"F0.imprint","IMPRINT",FACE,{"disambiguationData":[TD([[makeQuery(id+"F0.imprint","IMPRINT",EDGE,{"derivedFrom":subQ0}),-1.0]])]});}
            var Q37;
            {var subQ0=sQuery(id+"F0.wireOp",EDGE,"E15.right");Q37=makeQuery(id+"F0.imprint","IMPRINT",FACE,{"disambiguationData":[TD([[makeQuery(id+"F0.imprint","IMPRINT",EDGE,{"derivedFrom":subQ0}),1.0]])]});}
            var Q38;
            {var subQ0=sQuery(id+"F0.wireOp",EDGE,"E4.left");var subQ1=sQuery(id+"F0.wireOp",EDGE,"E4.top");var subQ2=makeQuery(id+"F0.imprint","INTERSECT",VERTEX,{"derivedFrom":[subQ1,subQ0]});Q38=makeQuery(id+"F0.imprint","IMPRINT",FACE,{"disambiguationData":[TD([[makeQuery(id+"F0.imprint","IMPRINT",EDGE,{"disambiguationData":[TD([[subQ2,-1.0]])],"derivedFrom":subQ1}),1.0]])]});}
            var Q39;
            {var subQ0=sQuery(id+"F0.wireOp",EDGE,"E29.top");var subQ1=sQuery(id+"F0.wireOp",EDGE,"E6.right");var subQ2=makeQuery(id+"F0.imprint","INTERSECT",VERTEX,{"derivedFrom":[subQ1,subQ0]});Q39=makeQuery(id+"F0.imprint","IMPRINT",FACE,{"disambiguationData":[TD([[makeQuery(id+"F0.imprint","IMPRINT",EDGE,{"disambiguationData":[TD([[subQ2,1.0]])],"derivedFrom":subQ1}),1.0]])]});}
            var Q40;
            {var subQ0=sQuery(id+"F0.wireOp",EDGE,"E40.top");var subQ1=sQuery(id+"F0.wireOp",EDGE,"E12.right");var subQ2=makeQuery(id+"F0.imprint","INTERSECT",VERTEX,{"derivedFrom":[subQ1,subQ0]});Q40=makeQuery(id+"F0.imprint","IMPRINT",FACE,{"disambiguationData":[TD([[makeQuery(id+"F0.imprint","IMPRINT",EDGE,{"disambiguationData":[TD([[subQ2,-1.0]])],"derivedFrom":subQ1}),-1.0]])]});}
            var Q41;
            {var subQ0=sQuery(id+"F0.wireOp",EDGE,"E19.top");Q41=makeQuery(id+"F0.imprint","IMPRINT",FACE,{"disambiguationData":[TD([[makeQuery(id+"F0.imprint","IMPRINT",EDGE,{"derivedFrom":subQ0}),1.0]])]});}
            var Q42;
            {var subQ0=sQuery(id+"F0.wireOp",EDGE,"E8.right");Q42=makeQuery(id+"F0.imprint","IMPRINT",FACE,{"disambiguationData":[TD([[makeQuery(id+"F0.imprint","IMPRINT",EDGE,{"derivedFrom":subQ0}),-1.0]])]});}
            var Q43;
            {var subQ0=sQuery(id+"F0.wireOp",EDGE,"E4.right");Q43=makeQuery(id+"F0.imprint","IMPRINT",FACE,{"disambiguationData":[TD([[makeQuery(id+"F0.imprint","IMPRINT",EDGE,{"derivedFrom":subQ0}),1.0]])]});}
            var Q44;
            {var subQ1=sQuery(id+"F0.wireOp",EDGE,"E26.top");Q44=makeQuery(id+"F0.imprint","IMPRINT",FACE,{"disambiguationData":[TD([[makeQuery(id+"F0.imprint","IMPRINT",EDGE,{"derivedFrom":subQ1}),1.0]])]});}
            var Q45;
            {var subQ0=sQuery(id+"F0.wireOp",EDGE,"E32.right");Q45=makeQuery(id+"F0.imprint","IMPRINT",FACE,{"disambiguationData":[TD([[makeQuery(id+"F0.imprint","IMPRINT",EDGE,{"derivedFrom":subQ0}),1.0]])]});}
            var Q46;
            {var subQ0=sQuery(id+"F0.wireOp",EDGE,"E20.bottom");var subQ1=sQuery(id+"F0.wireOp",EDGE,"E1.right");var subQ2=makeQuery(id+"F0.imprint","INTERSECT",VERTEX,{"derivedFrom":[subQ1,subQ0]});Q46=makeQuery(id+"F0.imprint","IMPRINT",FACE,{"disambiguationData":[TD([[makeQuery(id+"F0.imprint","IMPRINT",EDGE,{"disambiguationData":[TD([[subQ2,1.0]])],"derivedFrom":subQ1}),1.0]])]});}
            var Q47;
            {var subQ1=sQuery(id+"F0.wireOp",EDGE,"E37.bottom");Q47=makeQuery(id+"F0.imprint","IMPRINT",FACE,{"disambiguationData":[TD([[makeQuery(id+"F0.imprint","IMPRINT",EDGE,{"derivedFrom":subQ1}),-1.0]])]});}
            var Q48;
            {var subQ0=sQuery(id+"F0.wireOp",EDGE,"E13.left");var subQ1=sQuery(id+"F0.wireOp",EDGE,"E13.top");var subQ2=makeQuery(id+"F0.imprint","INTERSECT",VERTEX,{"derivedFrom":[subQ1,subQ0]});Q48=makeQuery(id+"F0.imprint","IMPRINT",FACE,{"disambiguationData":[TD([[makeQuery(id+"F0.imprint","IMPRINT",EDGE,{"disambiguationData":[TD([[subQ2,-1.0]])],"derivedFrom":subQ1}),1.0]])]});}
            var Q49;
            {var subQ0=sQuery(id+"F0.wireOp",EDGE,"E25.bottom");Q49=makeQuery(id+"F0.imprint","IMPRINT",FACE,{"disambiguationData":[TD([[makeQuery(id+"F0.imprint","IMPRINT",EDGE,{"derivedFrom":subQ0}),-1.0]])]});}
            var Q50;
            {var subQ1=sQuery(id+"F0.wireOp",EDGE,"E28.top");Q50=makeQuery(id+"F0.imprint","IMPRINT",FACE,{"disambiguationData":[TD([[makeQuery(id+"F0.imprint","IMPRINT",EDGE,{"derivedFrom":subQ1}),1.0]])]});}
            var Q51;
            {var subQ5=sQuery(id+"F0.wireOp",EDGE,"E39.top");Q51=makeQuery(id+"F0.imprint","IMPRINT",FACE,{"disambiguationData":[TD([[makeQuery(id+"F0.imprint","IMPRINT",EDGE,{"derivedFrom":subQ5}),1.0]])]});}
            var Q52;
            {var subQ0=sQuery(id+"F0.wireOp",EDGE,"E33.left");Q52=makeQuery(id+"F0.imprint","IMPRINT",FACE,{"disambiguationData":[TD([[makeQuery(id+"F0.imprint","IMPRINT",EDGE,{"derivedFrom":subQ0}),-1.0]])]});}
            var Q53;
            {var subQ0=sQuery(id+"F0.wireOp",EDGE,"E13.bottom");var subQ1=sQuery(id+"F0.wireOp",EDGE,"E12.left");var subQ2=makeQuery(id+"F0.imprint","INTERSECT",VERTEX,{"derivedFrom":[subQ1,subQ0]});Q53=makeQuery(id+"F0.imprint","IMPRINT",FACE,{"disambiguationData":[TD([[makeQuery(id+"F0.imprint","IMPRINT",EDGE,{"disambiguationData":[TD([[subQ2,1.0]])],"derivedFrom":subQ1}),-1.0]])]});}
            var Q54;
            {var subQ5=sQuery(id+"F0.wireOp",EDGE,"E30.left");Q54=makeQuery(id+"F0.imprint","IMPRINT",FACE,{"disambiguationData":[TD([[makeQuery(id+"F0.imprint","IMPRINT",EDGE,{"derivedFrom":subQ5}),-1.0]])]});}
            var Q55;
            {var subQ0=sQuery(id+"F0.wireOp",EDGE,"E13.bottom");var subQ1=sQuery(id+"F0.wireOp",EDGE,"E12.left");var subQ2=makeQuery(id+"F0.imprint","INTERSECT",VERTEX,{"derivedFrom":[subQ1,subQ0]});Q55=makeQuery(id+"F0.imprint","IMPRINT",FACE,{"disambiguationData":[TD([[makeQuery(id+"F0.imprint","IMPRINT",EDGE,{"disambiguationData":[TD([[subQ2,1.0]])],"derivedFrom":subQ1}),1.0]])]});}
            var Q56;
            {var subQ1=sQuery(id+"F0.wireOp",EDGE,"E20.top");Q56=makeQuery(id+"F0.imprint","IMPRINT",FACE,{"disambiguationData":[TD([[makeQuery(id+"F0.imprint","IMPRINT",EDGE,{"derivedFrom":subQ1}),-1.0]])]});}
            var Q57;
            {var subQ0=sQuery(id+"F0.wireOp",EDGE,"E7.right");Q57=makeQuery(id+"F0.imprint","IMPRINT",FACE,{"disambiguationData":[TD([[makeQuery(id+"F0.imprint","IMPRINT",EDGE,{"derivedFrom":subQ0}),1.0]])]});}
            var Q58;
            {var subQ1=sQuery(id+"F0.wireOp",EDGE,"E19.bottom");Q58=makeQuery(id+"F0.imprint","IMPRINT",FACE,{"disambiguationData":[TD([[makeQuery(id+"F0.imprint","IMPRINT",EDGE,{"derivedFrom":subQ1}),-1.0]])]});}
            var Q59;
            {var subQ0=sQuery(id+"F0.wireOp",EDGE,"E11.top");Q59=makeQuery(id+"F0.imprint","IMPRINT",FACE,{"disambiguationData":[TD([[makeQuery(id+"F0.imprint","IMPRINT",EDGE,{"derivedFrom":subQ0}),-1.0]])]});}
            var Q60;
            {var subQ1=sQuery(id+"F0.wireOp",EDGE,"E26.bottom");Q60=makeQuery(id+"F0.imprint","IMPRINT",FACE,{"disambiguationData":[TD([[makeQuery(id+"F0.imprint","IMPRINT",EDGE,{"derivedFrom":subQ1}),-1.0]])]});}
            var Q61;
            {var subQ0=sQuery(id+"F0.wireOp",EDGE,"E14.right");Q61=makeQuery(id+"F0.imprint","IMPRINT",FACE,{"disambiguationData":[TD([[makeQuery(id+"F0.imprint","IMPRINT",EDGE,{"derivedFrom":subQ0}),1.0]])]});}
            var Q62;
            {var subQ0=sQuery(id+"F0.wireOp",EDGE,"E5.right");Q62=makeQuery(id+"F0.imprint","IMPRINT",FACE,{"disambiguationData":[TD([[makeQuery(id+"F0.imprint","IMPRINT",EDGE,{"derivedFrom":subQ0}),-1.0]])]});}
            var Q63;
            {var subQ0=sQuery(id+"F0.wireOp",EDGE,"E4.bottom");var subQ1=sQuery(id+"F0.wireOp",EDGE,"E3.left");var subQ2=makeQuery(id+"F0.imprint","INTERSECT",VERTEX,{"derivedFrom":[subQ1,subQ0]});Q63=makeQuery(id+"F0.imprint","IMPRINT",FACE,{"disambiguationData":[TD([[makeQuery(id+"F0.imprint","IMPRINT",EDGE,{"disambiguationData":[TD([[subQ2,1.0]])],"derivedFrom":subQ1}),-1.0]])]});}
            var Q64;
            {var subQ0=sQuery(id+"F0.wireOp",EDGE,"E22.left");Q64=makeQuery(id+"F0.imprint","IMPRINT",FACE,{"disambiguationData":[TD([[makeQuery(id+"F0.imprint","IMPRINT",EDGE,{"derivedFrom":subQ0}),-1.0]])]});}
            var Q65;
            {var subQ0=sQuery(id+"F0.wireOp",EDGE,"E7.right");Q65=makeQuery(id+"F0.imprint","IMPRINT",FACE,{"disambiguationData":[TD([[makeQuery(id+"F0.imprint","IMPRINT",EDGE,{"derivedFrom":subQ0}),-1.0]])]});}
            var Q66;
            {var subQ0=sQuery(id+"F0.wireOp",EDGE,"E14.bottom");var subQ1=sQuery(id+"F0.wireOp",EDGE,"E1.left");var subQ2=makeQuery(id+"F0.imprint","INTERSECT",VERTEX,{"derivedFrom":[subQ1,subQ0]});Q66=makeQuery(id+"F0.imprint","IMPRINT",FACE,{"disambiguationData":[TD([[makeQuery(id+"F0.imprint","IMPRINT",EDGE,{"disambiguationData":[TD([[subQ2,-1.0]])],"derivedFrom":subQ1}),-1.0]])]});}
            var Q67;
            {var subQ3=sQuery(id+"F0.wireOp",EDGE,"E13.bottom");var subQ7=makeQuery(id+"F0.imprint","INTERSECT",VERTEX,{"derivedFrom":[sQuery(id+"F0.wireOp",EDGE,"E12.left"),subQ3]});Q67=makeQuery(id+"F0.imprint","IMPRINT",FACE,{"disambiguationData":[TD([[makeQuery(id+"F0.imprint","IMPRINT",EDGE,{"disambiguationData":[TD([[subQ7,1.0]])],"derivedFrom":subQ3}),-1.0]])]});}
            var Q68;
            {var subQ0=sQuery(id+"F0.wireOp",EDGE,"E34.bottom");Q68=makeQuery(id+"F0.imprint","IMPRINT",FACE,{"disambiguationData":[TD([[makeQuery(id+"F0.imprint","IMPRINT",EDGE,{"derivedFrom":subQ0}),-1.0]])]});}
            var Q69;
            {var subQ0=sQuery(id+"F0.wireOp",EDGE,"E3.bottom");Q69=makeQuery(id+"F0.imprint","IMPRINT",FACE,{"disambiguationData":[TD([[makeQuery(id+"F0.imprint","IMPRINT",EDGE,{"derivedFrom":subQ0}),-1.0]])]});}
            var Q70;
            {var subQ0=sQuery(id+"F0.wireOp",EDGE,"E35.bottom");Q70=makeQuery(id+"F0.imprint","IMPRINT",FACE,{"disambiguationData":[TD([[makeQuery(id+"F0.imprint","IMPRINT",EDGE,{"derivedFrom":subQ0}),-1.0]])]});}
            var Q71;
            {var subQ0=sQuery(id+"F0.wireOp",EDGE,"E21.left");Q71=makeQuery(id+"F0.imprint","IMPRINT",FACE,{"disambiguationData":[TD([[makeQuery(id+"F0.imprint","IMPRINT",EDGE,{"derivedFrom":subQ0}),1.0]])]});}
            var Q72;
            {var subQ0=sQuery(id+"F0.wireOp",EDGE,"E11.top");Q72=makeQuery(id+"F0.imprint","IMPRINT",FACE,{"disambiguationData":[TD([[makeQuery(id+"F0.imprint","IMPRINT",EDGE,{"derivedFrom":subQ0}),1.0]])]});}
            var Q73;
            {var subQ0=sQuery(id+"F0.wireOp",EDGE,"E23.left");Q73=makeQuery(id+"F0.imprint","IMPRINT",FACE,{"disambiguationData":[TD([[makeQuery(id+"F0.imprint","IMPRINT",EDGE,{"derivedFrom":subQ0}),1.0]])]});}
            var Q74;
            {var subQ1=sQuery(id+"F0.wireOp",EDGE,"E34.top");Q74=makeQuery(id+"F0.imprint","IMPRINT",FACE,{"disambiguationData":[TD([[makeQuery(id+"F0.imprint","IMPRINT",EDGE,{"derivedFrom":subQ1}),1.0]])]});}
            var Q75;
            {var subQ0=sQuery(id+"F0.wireOp",EDGE,"E2.bottom");Q75=makeQuery(id+"F0.imprint","IMPRINT",FACE,{"disambiguationData":[TD([[makeQuery(id+"F0.imprint","IMPRINT",EDGE,{"derivedFrom":subQ0}),1.0]])]});}
            var Q76;
            {var subQ0=sQuery(id+"F0.wireOp",EDGE,"E39.bottom");var subQ1=sQuery(id+"F0.wireOp",EDGE,"E3.right");var subQ2=makeQuery(id+"F0.imprint","INTERSECT",VERTEX,{"derivedFrom":[subQ1,subQ0]});Q76=makeQuery(id+"F0.imprint","IMPRINT",FACE,{"disambiguationData":[TD([[makeQuery(id+"F0.imprint","IMPRINT",EDGE,{"disambiguationData":[TD([[subQ2,-1.0]])],"derivedFrom":subQ1}),1.0]])]});}
            var Q77;
            {var subQ0=sQuery(id+"F0.wireOp",EDGE,"E40.top");var subQ1=sQuery(id+"F0.wireOp",EDGE,"E12.right");var subQ2=makeQuery(id+"F0.imprint","INTERSECT",VERTEX,{"derivedFrom":[subQ1,subQ0]});Q77=makeQuery(id+"F0.imprint","IMPRINT",FACE,{"disambiguationData":[TD([[makeQuery(id+"F0.imprint","IMPRINT",EDGE,{"disambiguationData":[TD([[subQ2,-1.0]])],"derivedFrom":subQ1}),1.0]])]});}
            var Q78;
            {var subQ1=sQuery(id+"F0.wireOp",EDGE,"E36.top");Q78=makeQuery(id+"F0.imprint","IMPRINT",FACE,{"disambiguationData":[TD([[makeQuery(id+"F0.imprint","IMPRINT",EDGE,{"derivedFrom":subQ1}),-1.0]])]});}
            var Q79;
            {var subQ0=sQuery(id+"F0.wireOp",EDGE,"E31.right");Q79=makeQuery(id+"F0.imprint","IMPRINT",FACE,{"disambiguationData":[TD([[makeQuery(id+"F0.imprint","IMPRINT",EDGE,{"derivedFrom":subQ0}),-1.0]])]});}
            var Q80;
            {var subQ0=sQuery(id+"F0.wireOp",EDGE,"E14.left");var subQ1=sQuery(id+"F0.wireOp",EDGE,"E14.top");var subQ2=makeQuery(id+"F0.imprint","INTERSECT",VERTEX,{"derivedFrom":[subQ1,subQ0]});Q80=makeQuery(id+"F0.imprint","IMPRINT",FACE,{"disambiguationData":[TD([[makeQuery(id+"F0.imprint","IMPRINT",EDGE,{"disambiguationData":[TD([[subQ2,-1.0]])],"derivedFrom":subQ1}),-1.0]])]});}
            var Q81;
            {var subQ0=sQuery(id+"F0.wireOp",EDGE,"E31.left");Q81=makeQuery(id+"F0.imprint","IMPRINT",FACE,{"disambiguationData":[TD([[makeQuery(id+"F0.imprint","IMPRINT",EDGE,{"derivedFrom":subQ0}),1.0]])]});}
            var Q82;
            {var subQ5=sQuery(id+"F0.wireOp",EDGE,"E38.right");Q82=makeQuery(id+"F0.imprint","IMPRINT",FACE,{"disambiguationData":[TD([[makeQuery(id+"F0.imprint","IMPRINT",EDGE,{"derivedFrom":subQ5}),-1.0]])]});}
            var Q83;
            {var subQ0=sQuery(id+"F0.wireOp",EDGE,"E22.right");Q83=makeQuery(id+"F0.imprint","IMPRINT",FACE,{"disambiguationData":[TD([[makeQuery(id+"F0.imprint","IMPRINT",EDGE,{"derivedFrom":subQ0}),1.0]])]});}
            var Q84;
            {var subQ0=sQuery(id+"F0.wireOp",EDGE,"E13.right");Q84=makeQuery(id+"F0.imprint","IMPRINT",FACE,{"disambiguationData":[TD([[makeQuery(id+"F0.imprint","IMPRINT",EDGE,{"derivedFrom":subQ0}),-1.0]])]});}
            var Q85;
            {var subQ1=sQuery(id+"F0.wireOp",EDGE,"E12.right");var subQ3=sQuery(id+"F0.wireOp",EDGE,"E33.top");var subQ4=makeQuery(id+"F0.imprint","INTERSECT",VERTEX,{"derivedFrom":[subQ1,subQ3]});Q85=makeQuery(id+"F0.imprint","IMPRINT",FACE,{"disambiguationData":[TD([[makeQuery(id+"F0.imprint","IMPRINT",EDGE,{"disambiguationData":[TD([[subQ4,-1.0]])],"derivedFrom":subQ3}),-1.0]])]});}
            var Q86;
            {var subQ0=sQuery(id+"F0.wireOp",EDGE,"E32.left");Q86=makeQuery(id+"F0.imprint","IMPRINT",FACE,{"disambiguationData":[TD([[makeQuery(id+"F0.imprint","IMPRINT",EDGE,{"derivedFrom":subQ0}),-1.0]])]});}
            var Q87;
            {var subQ0=sQuery(id+"F0.wireOp",EDGE,"E6.top");Q87=makeQuery(id+"F0.imprint","IMPRINT",FACE,{"disambiguationData":[TD([[makeQuery(id+"F0.imprint","IMPRINT",EDGE,{"derivedFrom":subQ0}),1.0]])]});}
            var Q88;
            {var subQ0=sQuery(id+"F0.wireOp",EDGE,"E17.right");Q88=makeQuery(id+"F0.imprint","IMPRINT",FACE,{"disambiguationData":[TD([[makeQuery(id+"F0.imprint","IMPRINT",EDGE,{"derivedFrom":subQ0}),-1.0]])]});}
            var Q89;
            {var subQ0=sQuery(id+"F0.wireOp",EDGE,"E20.bottom");var subQ1=sQuery(id+"F0.wireOp",EDGE,"E1.right");var subQ2=makeQuery(id+"F0.imprint","INTERSECT",VERTEX,{"derivedFrom":[subQ1,subQ0]});Q89=makeQuery(id+"F0.imprint","IMPRINT",FACE,{"disambiguationData":[TD([[makeQuery(id+"F0.imprint","IMPRINT",EDGE,{"disambiguationData":[TD([[subQ2,1.0]])],"derivedFrom":subQ1}),-1.0]])]});}
            var Q90;
            {var subQ0=sQuery(id+"F0.wireOp",EDGE,"E7.bottom");var subQ5=sQuery(id+"F0.wireOp",EDGE,"E29.right");var subQ7=makeQuery(id+"F0.imprint","INTERSECT",VERTEX,{"derivedFrom":[subQ0,subQ5]});Q90=makeQuery(id+"F0.imprint","IMPRINT",FACE,{"disambiguationData":[TD([[makeQuery(id+"F0.imprint","IMPRINT",EDGE,{"disambiguationData":[TD([[subQ7,-1.0]])],"derivedFrom":subQ5}),-1.0]])]});}
            var Q91;
            {var subQ0=sQuery(id+"F0.wireOp",EDGE,"E21.right");Q91=makeQuery(id+"F0.imprint","IMPRINT",FACE,{"disambiguationData":[TD([[makeQuery(id+"F0.imprint","IMPRINT",EDGE,{"derivedFrom":subQ0}),-1.0]])]});}
            var Q92;
            {var subQ0=sQuery(id+"F0.wireOp",EDGE,"E7.bottom");var subQ1=sQuery(id+"F0.wireOp",EDGE,"E6.left");var subQ2=makeQuery(id+"F0.imprint","INTERSECT",VERTEX,{"derivedFrom":[subQ1,subQ0]});Q92=makeQuery(id+"F0.imprint","IMPRINT",FACE,{"disambiguationData":[TD([[makeQuery(id+"F0.imprint","IMPRINT",EDGE,{"disambiguationData":[TD([[subQ2,-1.0]])],"derivedFrom":subQ1}),1.0]])]});}
            var Q93;
            {var subQ0=sQuery(id+"F0.wireOp",EDGE,"E16.right");Q93=makeQuery(id+"F0.imprint","IMPRINT",FACE,{"disambiguationData":[TD([[makeQuery(id+"F0.imprint","IMPRINT",EDGE,{"derivedFrom":subQ0}),-1.0]])]});}
            var Q94;
            {var subQ0=sQuery(id+"F0.wireOp",EDGE,"E4.bottom");var subQ1=sQuery(id+"F0.wireOp",EDGE,"E3.left");var subQ2=makeQuery(id+"F0.imprint","INTERSECT",VERTEX,{"derivedFrom":[subQ1,subQ0]});Q94=makeQuery(id+"F0.imprint","IMPRINT",FACE,{"disambiguationData":[TD([[makeQuery(id+"F0.imprint","IMPRINT",EDGE,{"disambiguationData":[TD([[subQ2,1.0]])],"derivedFrom":subQ1}),1.0]])]});}
            var Q95;
            {var subQ0=sQuery(id+"F0.wireOp",EDGE,"E9.right");Q95=makeQuery(id+"F0.imprint","IMPRINT",FACE,{"disambiguationData":[TD([[makeQuery(id+"F0.imprint","IMPRINT",EDGE,{"derivedFrom":subQ0}),1.0]])]});}
            var Q96;
            {var subQ0=sQuery(id+"F0.wireOp",EDGE,"E14.right");Q96=makeQuery(id+"F0.imprint","IMPRINT",FACE,{"disambiguationData":[TD([[makeQuery(id+"F0.imprint","IMPRINT",EDGE,{"derivedFrom":subQ0}),-1.0]])]});}
            var Q97;
            {var subQ0=sQuery(id+"F0.wireOp",EDGE,"E14.bottom");var subQ1=sQuery(id+"F0.wireOp",EDGE,"E1.left");var subQ2=makeQuery(id+"F0.imprint","INTERSECT",VERTEX,{"derivedFrom":[subQ1,subQ0]});Q97=makeQuery(id+"F0.imprint","IMPRINT",FACE,{"disambiguationData":[TD([[makeQuery(id+"F0.imprint","IMPRINT",EDGE,{"disambiguationData":[TD([[subQ2,-1.0]])],"derivedFrom":subQ1}),1.0]])]});}
            var Q98;
            {var subQ0=sQuery(id+"F0.wireOp",EDGE,"E35.top");Q98=makeQuery(id+"F0.imprint","IMPRINT",FACE,{"disambiguationData":[TD([[makeQuery(id+"F0.imprint","IMPRINT",EDGE,{"derivedFrom":subQ0}),1.0]])]});}
            var Q99;
            {var subQ1=sQuery(id+"F0.wireOp",EDGE,"E36.bottom");Q99=makeQuery(id+"F0.imprint","IMPRINT",FACE,{"disambiguationData":[TD([[makeQuery(id+"F0.imprint","IMPRINT",EDGE,{"derivedFrom":subQ1}),1.0]])]});}
            var Q100;
            {var subQ0=sQuery(id+"F0.wireOp",EDGE,"E39.left");var subQ5=sQuery(id+"F0.wireOp",EDGE,"E23.bottom");var subQ6=makeQuery(id+"F0.imprint","INTERSECT",VERTEX,{"derivedFrom":[subQ5,subQ0]});Q100=makeQuery(id+"F0.imprint","IMPRINT",FACE,{"disambiguationData":[TD([[makeQuery(id+"F0.imprint","IMPRINT",EDGE,{"disambiguationData":[TD([[subQ6,-1.0]])],"derivedFrom":subQ5}),-1.0]])]});}
            var Q101;
            {var subQ0=sQuery(id+"F0.wireOp",EDGE,"E13.left");var subQ5=sQuery(id+"F0.wireOp",EDGE,"E33.bottom");var subQ7=makeQuery(id+"F0.imprint","INTERSECT",VERTEX,{"derivedFrom":[subQ0,subQ5]});Q101=makeQuery(id+"F0.imprint","IMPRINT",FACE,{"disambiguationData":[TD([[makeQuery(id+"F0.imprint","IMPRINT",EDGE,{"disambiguationData":[TD([[subQ7,-1.0]])],"derivedFrom":subQ5}),1.0]])]});}
            var Q102;
            {var subQ5=sQuery(id+"F0.wireOp",EDGE,"E14.bottom");var subQ7=makeQuery(id+"F0.imprint","INTERSECT",VERTEX,{"derivedFrom":[sQuery(id+"F0.wireOp",EDGE,"E1.left"),subQ5]});Q102=makeQuery(id+"F0.imprint","IMPRINT",FACE,{"disambiguationData":[TD([[makeQuery(id+"F0.imprint","IMPRINT",EDGE,{"disambiguationData":[TD([[subQ7,1.0]])],"derivedFrom":subQ5}),1.0]])]});}
            var Q103;
            {var subQ0=sQuery(id+"F0.wireOp",EDGE,"E3.bottom");Q103=makeQuery(id+"F0.imprint","IMPRINT",FACE,{"disambiguationData":[TD([[makeQuery(id+"F0.imprint","IMPRINT",EDGE,{"derivedFrom":subQ0}),1.0]])]});}
            var Q104;
            {var subQ0=sQuery(id+"F0.wireOp",EDGE,"E6.top");Q104=makeQuery(id+"F0.imprint","IMPRINT",FACE,{"disambiguationData":[TD([[makeQuery(id+"F0.imprint","IMPRINT",EDGE,{"derivedFrom":subQ0}),-1.0]])]});}
            var Q105;
            {var subQ1=sQuery(id+"F0.wireOp",EDGE,"E7.bottom");var subQ3=sQuery(id+"F0.wireOp",EDGE,"E29.right");var subQ4=makeQuery(id+"F0.imprint","INTERSECT",VERTEX,{"derivedFrom":[subQ1,subQ3]});Q105=makeQuery(id+"F0.imprint","IMPRINT",FACE,{"disambiguationData":[TD([[makeQuery(id+"F0.imprint","IMPRINT",EDGE,{"disambiguationData":[TD([[subQ4,1.0]])],"derivedFrom":subQ3}),-1.0]])]});}
            var Q106;
            {var subQ0=sQuery(id+"F0.wireOp",EDGE,"E2.bottom");Q106=makeQuery(id+"F0.imprint","IMPRINT",FACE,{"disambiguationData":[TD([[makeQuery(id+"F0.imprint","IMPRINT",EDGE,{"derivedFrom":subQ0}),-1.0]])]});}
            var Q107;
            {var subQ0=sQuery(id+"F0.wireOp",EDGE,"E39.bottom");var subQ1=sQuery(id+"F0.wireOp",EDGE,"E3.right");var subQ2=makeQuery(id+"F0.imprint","INTERSECT",VERTEX,{"derivedFrom":[subQ1,subQ0]});Q107=makeQuery(id+"F0.imprint","IMPRINT",FACE,{"disambiguationData":[TD([[makeQuery(id+"F0.imprint","IMPRINT",EDGE,{"disambiguationData":[TD([[subQ2,-1.0]])],"derivedFrom":subQ1}),-1.0]])]});}
            var Q108;
            {var subQ0=sQuery(id+"F0.wireOp",EDGE,"E16.right");Q108=makeQuery(id+"F0.imprint","IMPRINT",FACE,{"disambiguationData":[TD([[makeQuery(id+"F0.imprint","IMPRINT",EDGE,{"derivedFrom":subQ0}),1.0]])]});}
            var Q109;
            {var subQ0=sQuery(id+"F0.wireOp",EDGE,"E14.bottom");var subQ5=sQuery(id+"F0.wireOp",EDGE,"E20.right");var subQ6=makeQuery(id+"F0.imprint","INTERSECT",VERTEX,{"derivedFrom":[subQ0,subQ5]});Q109=makeQuery(id+"F0.imprint","IMPRINT",FACE,{"disambiguationData":[TD([[makeQuery(id+"F0.imprint","IMPRINT",EDGE,{"disambiguationData":[TD([[subQ6,1.0]])],"derivedFrom":subQ5}),1.0]])]});}
            var Q110;
            {var subQ0=sQuery(id+"F0.wireOp",EDGE,"E17.right");Q110=makeQuery(id+"F0.imprint","IMPRINT",FACE,{"disambiguationData":[TD([[makeQuery(id+"F0.imprint","IMPRINT",EDGE,{"derivedFrom":subQ0}),1.0]])]});}
            var Q111;
            {var subQ5=sQuery(id+"F0.wireOp",EDGE,"E4.bottom");var subQ6=makeQuery(id+"F0.imprint","INTERSECT",VERTEX,{"derivedFrom":[sQuery(id+"F0.wireOp",EDGE,"E3.left"),subQ5]});Q111=makeQuery(id+"F0.imprint","IMPRINT",FACE,{"disambiguationData":[TD([[makeQuery(id+"F0.imprint","IMPRINT",EDGE,{"disambiguationData":[TD([[subQ6,1.0]])],"derivedFrom":subQ5}),-1.0]])]});}
            var Q112;
            {var subQ0=sQuery(id+"F0.wireOp",EDGE,"E38.bottom");var subQ1=sQuery(id+"F0.wireOp",EDGE,"E20.left");var subQ2=makeQuery(id+"F0.imprint","INTERSECT",VERTEX,{"derivedFrom":[subQ1,subQ0]});Q112=makeQuery(id+"F0.imprint","IMPRINT",FACE,{"disambiguationData":[TD([[makeQuery(id+"F0.imprint","IMPRINT",EDGE,{"disambiguationData":[TD([[subQ2,-1.0]])],"derivedFrom":subQ1}),-1.0]])]});}
            var Q113;
            {var subQ1=sQuery(id+"F0.wireOp",EDGE,"E3.right");var subQ3=sQuery(id+"F0.wireOp",EDGE,"E23.bottom");var subQ4=makeQuery(id+"F0.imprint","INTERSECT",VERTEX,{"derivedFrom":[subQ1,subQ3]});Q113=makeQuery(id+"F0.imprint","IMPRINT",FACE,{"disambiguationData":[TD([[makeQuery(id+"F0.imprint","IMPRINT",EDGE,{"disambiguationData":[TD([[subQ4,-1.0]])],"derivedFrom":subQ3}),-1.0]])]});}
            var Q114;
            {var subQ1=sQuery(id+"F0.wireOp",EDGE,"E29.left");var subQ7=sQuery(id+"F0.wireOp",EDGE,"E30.top");var subQ9=makeQuery(id+"F0.imprint","INTERSECT",VERTEX,{"derivedFrom":[subQ1,subQ7]});Q114=makeQuery(id+"F0.imprint","IMPRINT",FACE,{"disambiguationData":[TD([[makeQuery(id+"F0.imprint","IMPRINT",EDGE,{"disambiguationData":[TD([[subQ9,-1.0]])],"derivedFrom":subQ1}),1.0]])]});}
            var Q115;
            {var subQ0=sQuery(id+"F0.wireOp",EDGE,"E40.left");var subQ5=sQuery(id+"F0.wireOp",EDGE,"E33.bottom");var subQ6=makeQuery(id+"F0.imprint","INTERSECT",VERTEX,{"derivedFrom":[subQ5,subQ0]});Q115=makeQuery(id+"F0.imprint","IMPRINT",FACE,{"disambiguationData":[TD([[makeQuery(id+"F0.imprint","IMPRINT",EDGE,{"disambiguationData":[TD([[subQ6,-1.0]])],"derivedFrom":subQ5}),1.0]])]});}
            var Q116;
            {var subQ0=sQuery(id+"F0.wireOp",EDGE,"E4.left");var subQ5=sQuery(id+"F0.wireOp",EDGE,"E23.top");var subQ7=makeQuery(id+"F0.imprint","INTERSECT",VERTEX,{"derivedFrom":[subQ0,subQ5]});Q116=makeQuery(id+"F0.imprint","IMPRINT",FACE,{"disambiguationData":[TD([[makeQuery(id+"F0.imprint","IMPRINT",EDGE,{"disambiguationData":[TD([[subQ7,-1.0]])],"derivedFrom":subQ5}),1.0]])]});}
            var Q117;
            {var subQ1=sQuery(id+"F0.wireOp",EDGE,"E14.bottom");var subQ3=sQuery(id+"F0.wireOp",EDGE,"E20.right");var subQ4=makeQuery(id+"F0.imprint","INTERSECT",VERTEX,{"derivedFrom":[subQ1,subQ3]});Q117=makeQuery(id+"F0.imprint","IMPRINT",FACE,{"disambiguationData":[TD([[makeQuery(id+"F0.imprint","IMPRINT",EDGE,{"disambiguationData":[TD([[subQ4,-1.0]])],"derivedFrom":subQ3}),1.0]])]});}
            extrude(context, id + "F1", {"entities" : qUnion([Q0, Q1, Q2, Q3, Q4, Q5, Q6, Q7, Q8, Q9, Q10, Q11, Q12, Q13, Q14, Q15, Q16, Q17, Q18, Q19, Q20, Q21, Q22, Q23, Q24, Q25, Q26, Q27, Q28, Q29, Q30, Q31, Q32, Q33, Q34, Q35, Q36, Q37, Q38, Q39, Q40, Q41, Q42, Q43, Q44, Q45, Q46, Q47, Q48, Q49, Q50, Q51, Q52, Q53, Q54, Q55, Q56, Q57, Q58, Q59, Q60, Q61, Q62, Q63, Q64, Q65, Q66, Q67, Q68, Q69, Q70, Q71, Q72, Q73, Q74, Q75, Q76, Q77, Q78, Q79, Q80, Q81, Q82, Q83, Q84, Q85, Q86, Q87, Q88, Q89, Q90, Q91, Q92, Q93, Q94, Q95, Q96, Q97, Q98, Q99, Q100, Q101, Q102, Q103, Q104, Q105, Q106, Q107, Q108, Q109, Q110, Q111, Q112, Q113, Q114, Q115, Q116, Q117]), "flatOperationType" : FlatOperationType.REMOVE, "depth" : 300 * mm, "offsetDistance" : 25 * mm, "domain" : OperationDomain.MODEL});
        }
    });
